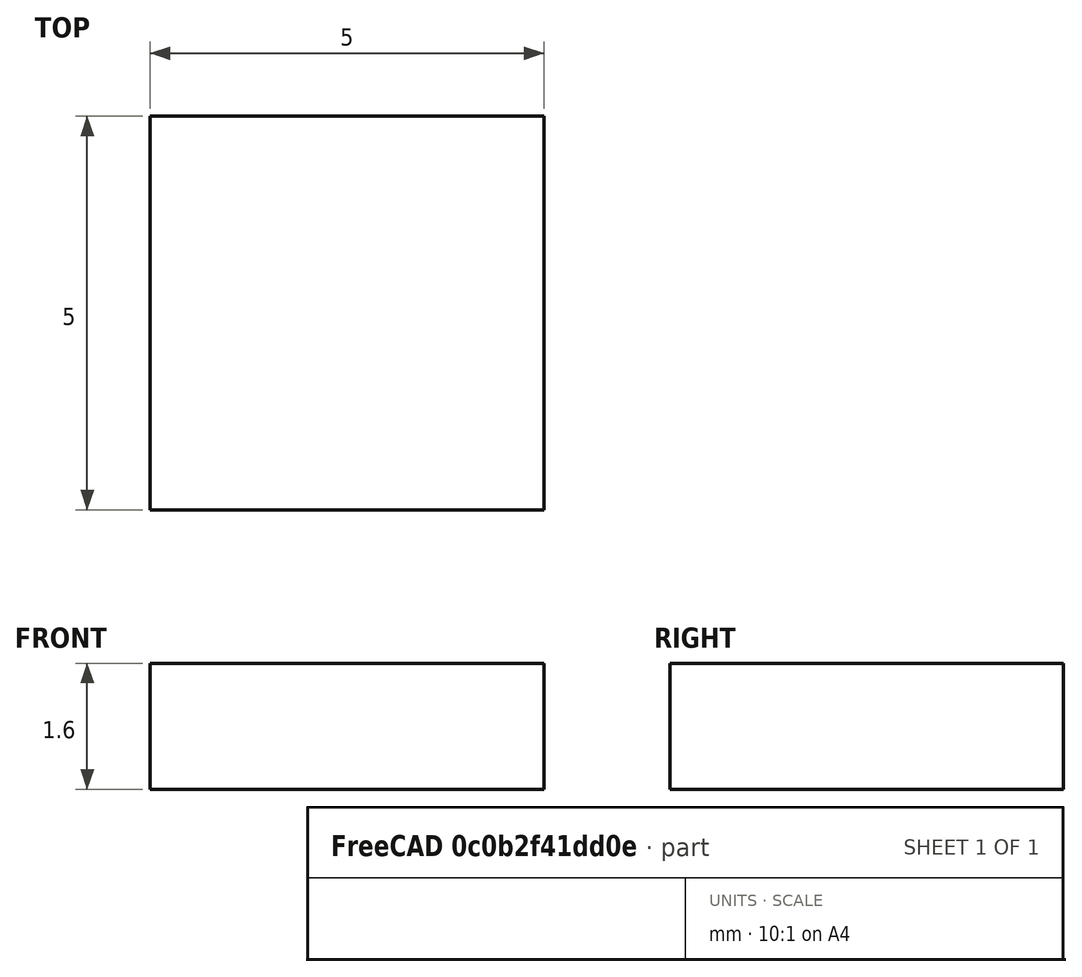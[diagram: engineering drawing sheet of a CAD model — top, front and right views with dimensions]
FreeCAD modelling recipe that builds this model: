
FCSTD DOCUMENT  (FreeCAD 0.16R6704 (Git))
Label: ws2812b
License: All rights reserved
LicenseURL: http://en.wikipedia.org/wiki/All_rights_reserved
objects: Sketcher::SketchObject×1, PartDesign::Pad×1
note: 3 computed .brp shape members not serialized (recipe doc carries the construction recipe); baked Part::Feature solids carry a one-line shape summary decoded from their .brp

FEATURE [Sketcher::SketchObject] Sketch
  sketch-geometry (4):
    g0: LineSegment StartX=-2.5 StartY=2.5 StartZ=0 EndX=2.5 EndY=2.5 EndZ=0
    g1: LineSegment StartX=2.5 StartY=2.5 StartZ=0 EndX=2.5 EndY=-2.5 EndZ=0
    g2: LineSegment StartX=2.5 StartY=-2.5 StartZ=0 EndX=-2.5 EndY=-2.5 EndZ=0
    g3: LineSegment StartX=-2.5 StartY=-2.5 StartZ=0 EndX=-2.5 EndY=2.5 EndZ=0
  constraints (12):
    c: Coincident(g0,g1)
    c: Coincident(g1,g2)
    c: Coincident(g2,g3)
    c: Coincident(g3,g0)
    c: Horizontal(g0)
    c: Horizontal(g2)
    c: Vertical(g1)
    c: Vertical(g3)
    c: DistanceX(g0,g0) = 5
    c: DistanceY(g3,g3) = 5
    c: Symmetric(g0,g0,g-2)
    c: Symmetric(g0,g2,g-1)
FEATURE [PartDesign::Pad] Pad  label="ws2812b"
  Length = 1.6
  Length2 = 100
  Sketch = -> Sketch
  Type = 0
